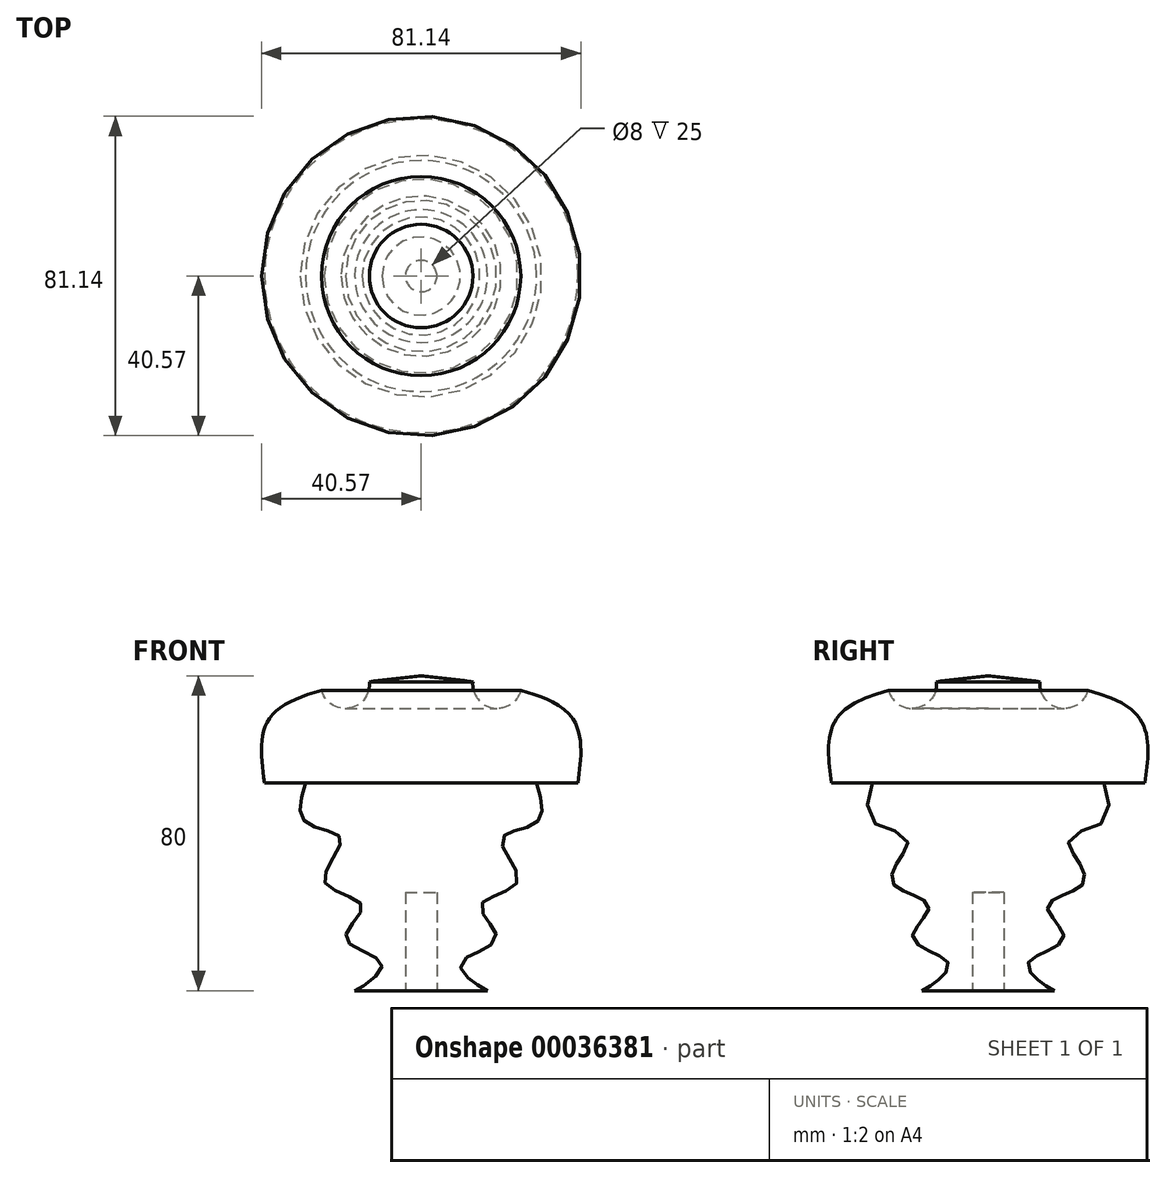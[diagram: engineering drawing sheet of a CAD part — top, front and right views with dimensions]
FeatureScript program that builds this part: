
annotation { "Feature Type Name" : "Feature", "Feature Type Description" : "" }
export const myFeature = defineFeature(function(context is Context, id is Id, definition is map)
    precondition{}
    {
        {
            var Q0;
            Q0=qCreatedBy(makeId("Front.planeOp"),FACE);
            var sketch = newSketch(context, id + "F0", { "sketchPlane" : qUnion([Q0])});
            skLineSegment(sketch, "E0", {"start": v(0, 0) * mm, "end": v(0, 80) * mm});
            skFitSpline(sketch, "E1", {"points": [v(0, 80) * mm, v(37.78, 70.08) * mm, v(39.82, 52.73) * mm], "startDerivative": vector(80.4, -8.55) * mm, "endDerivative": vector(-6.52, -48.65) * mm});
            skLineSegment(sketch, "E2", {"start": v(39.82, 52.73) * mm, "end": v(29.36, 52.73) * mm});
            skFitSpline(sketch, "E3", {"points": [v(29.36, 52.73) * mm, v(29.36, 42.78) * mm, v(20.43, 38.44) * mm, v(24.51, 27.72) * mm, v(15.07, 21.6) * mm, v(19.15, 13.18) * mm, v(9.97, 6.55) * mm, v(16.86, 0) * mm, v(17.11, 0) * mm], "startDerivative": vector(26.34, -87.28) * mm, "endDerivative": vector(5.43, 4.1) * mm});
            skLineSegment(sketch, "E4", {"start": v(17.11, 0) * mm, "end": v(0, 0) * mm});
            skSolve(sketch);
        }
        {
            var Q0;
            {var subQ3=sQuery(id+"F0.wireOp",EDGE,"E0");Q0=makeQuery(id+"F0.imprint","IMPRINT",FACE,{"disambiguationData":[TD([[makeQuery(id+"F0.imprint","IMPRINT",EDGE,{"derivedFrom":subQ3}),-1.0]])]});}
            var Q1;
            Q1=sQuery(id+"F0.wireOp",EDGE,"E0");
            revolve(context, id + "F1", {"entities" : qUnion([Q0]), "axis" : qUnion([Q1]), "revolveType" : RevolveType.FULL});
        }
        {
            var Q0;
            Q0=qCreatedBy(makeId("Front.planeOp"),FACE);
            var sketch = newSketch(context, id + "F2", { "sketchPlane" : qUnion([Q0])});
            skCircle(sketch, "E5", {"center": v(19.33, 77.91) * mm, "radius": 6.21 * mm});
            skSolve(sketch);
        }
        {
            var Q0;
            Q0=makeQuery(id+"F2.imprint","IMPRINT",FACE,{"disambiguationData":[TD([[makeQuery(id+"F2.imprint","IMPRINT",EDGE,{"derivedFrom":sQuery(id+"F2.wireOp",EDGE,"E5")}),1.0]])]});
            var Q1;
            Q1=sQuery(id+"F0.wireOp",EDGE,"E0");
            revolve(context, id + "F3", {"operationType" : NewBodyOperationType.REMOVE, "entities" : qUnion([Q0]), "axis" : qUnion([Q1]), "revolveType" : RevolveType.FULL, "oppositeDirection" : true});
        }
        {
            var Q0;
            Q0=makeQuery(id+"F1.opRevolve","SWEPT_FACE",FACE,{"disambiguationData":[OSD([sQuery(id+"F0.wireOp",EDGE,"E4")])]});
            var sketch = newSketch(context, id + "F4", { "sketchPlane" : qUnion([Q0])});
            skCircle(sketch, "E6", {"center": v(0, 0) * mm, "radius": 4 * mm});
            skSolve(sketch);
        }
        {
            var Q0;
            Q0=makeQuery(id+"F4.imprint","IMPRINT",FACE,{"disambiguationData":[TD([[makeQuery(id+"F4.imprint","IMPRINT",EDGE,{"derivedFrom":sQuery(id+"F4.wireOp",EDGE,"E6")}),1.0]])]});
            extrude(context, id + "F5", {"entities" : qUnion([Q0]), "operationType" : NewBodyOperationType.REMOVE, "oppositeDirection" : true, "depth" : 25 * mm});
        }
    });
